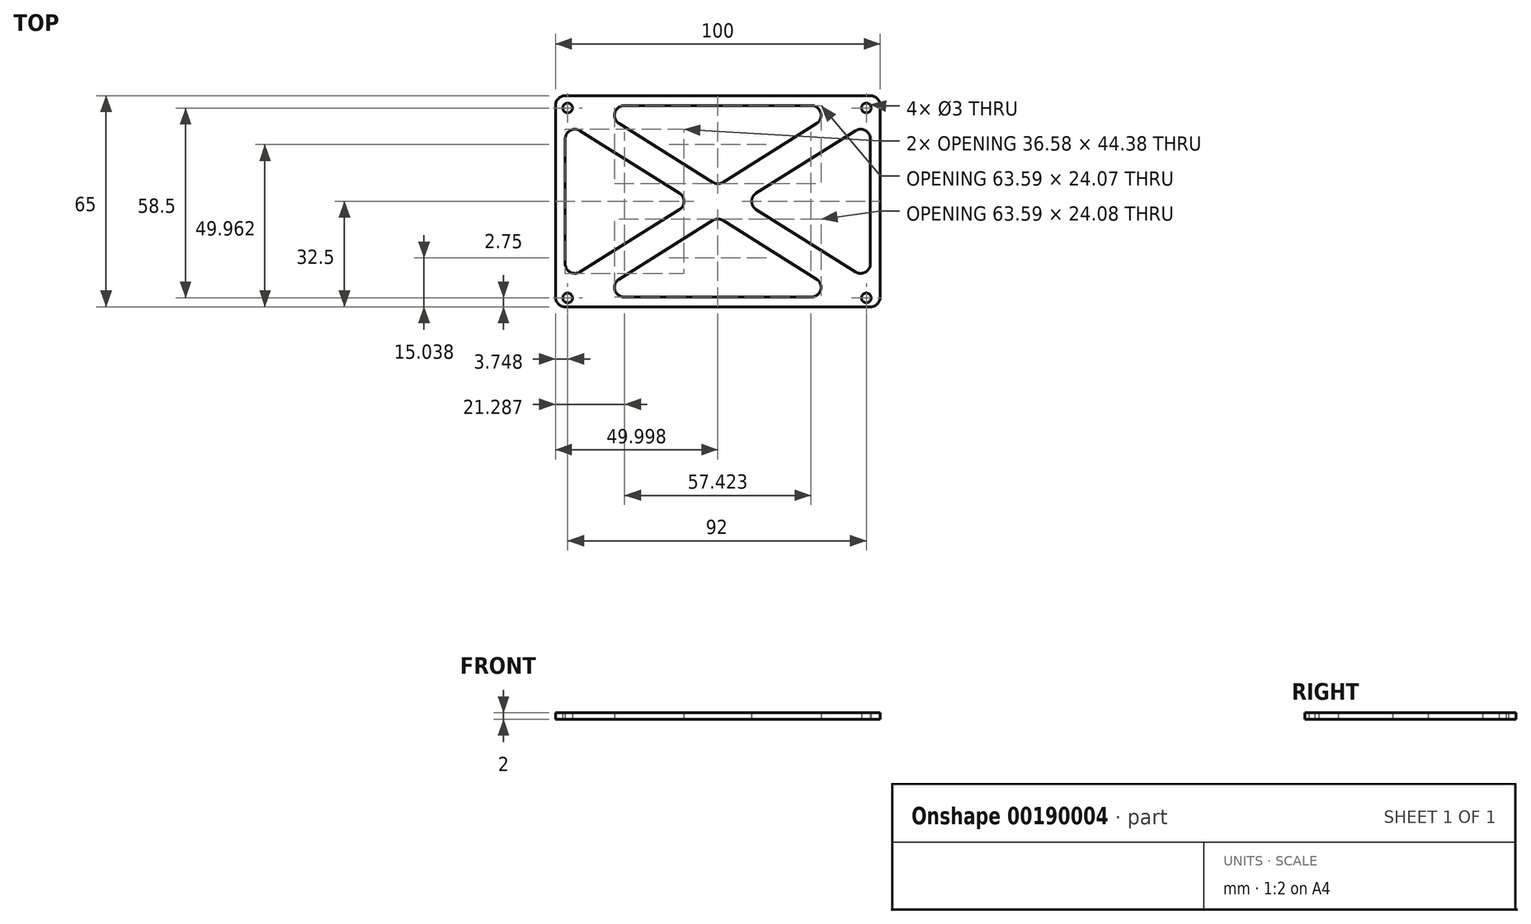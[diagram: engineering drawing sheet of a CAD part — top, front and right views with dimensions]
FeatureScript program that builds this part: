
annotation { "Feature Type Name" : "Feature", "Feature Type Description" : "" }
export const myFeature = defineFeature(function(context is Context, id is Id, definition is map)
    precondition{}
    {
        {
            var Q0;
            Q0=qCreatedBy(makeId("Top.planeOp"),FACE);
            var sketch = newSketch(context, id + "F0", { "sketchPlane" : qUnion([Q0])});
            skCircle(sketch, "E0", {"center": v(-51.9, 0) * mm, "radius": 1.5 * mm});
            skCircle(sketch, "E1", {"center": v(40.1, 0) * mm, "radius": 1.5 * mm});
            skCircle(sketch, "E2", {"center": v(-51.9, -58.5) * mm, "radius": 1.5 * mm});
            skCircle(sketch, "E3", {"center": v(40.1, -58.5) * mm, "radius": 1.5 * mm});
            skLineSegment(sketch, "E4", {"start": v(-52.65, 3.75) * mm, "end": v(-49.65, 3.75) * mm});
            skLineSegment(sketch, "E5", {"start": v(44.35, 0.75) * mm, "end": v(44.35, -2.25) * mm});
            skLineSegment(sketch, "E6", {"start": v(41.35, -61.25) * mm, "end": v(38.35, -61.25) * mm});
            skLineSegment(sketch, "E7", {"start": v(-55.65, -58.25) * mm, "end": v(-55.65, -55.25) * mm});
            skPoint(sketch, "E8.visualSharp", {"position": v(-55.65, 3.75) * mm});
            skArc(sketch, "E8.filletArc", {"start": v(-52.65, 3.75) * mm, "mid": v(-54.77, 2.87) * mm, "end": v(-55.65, 0.75) * mm});
            skPoint(sketch, "E9.visualSharp", {"position": v(44.35, 3.75) * mm});
            skArc(sketch, "E9.filletArc", {"start": v(44.35, 0.75) * mm, "mid": v(43.47, 2.87) * mm, "end": v(41.35, 3.75) * mm});
            skPoint(sketch, "E10.visualSharp", {"position": v(44.35, -61.25) * mm});
            skArc(sketch, "E10.filletArc", {"start": v(41.35, -61.25) * mm, "mid": v(43.47, -60.37) * mm, "end": v(44.35, -58.25) * mm});
            skPoint(sketch, "E11.visualSharp", {"position": v(-55.65, -61.25) * mm});
            skArc(sketch, "E11.filletArc", {"start": v(-55.65, -58.25) * mm, "mid": v(-54.77, -60.37) * mm, "end": v(-52.65, -61.25) * mm});
            skLineSegment(sketch, "E12", {"start": v(-36.04, -4.8) * mm, "end": v(-7.25, -22.87) * mm});
            skLineSegment(sketch, "E13", {"start": v(-48.06, -7.02) * mm, "end": v(-17.48, -26.2) * mm});
            skLineSegment(sketch, "E14", {"start": v(-48.06, -50.48) * mm, "end": v(-17.48, -31.3) * mm});
            skLineSegment(sketch, "E15", {"start": v(-36.04, -52.7) * mm, "end": v(-7.25, -34.63) * mm});
            skLineSegment(sketch, "E16.trimOffspring", {"start": v(-4.06, -22.87) * mm, "end": v(24.74, -4.8) * mm});
            skLineSegment(sketch, "E17.trimOffspring", {"start": v(6.18, -31.3) * mm, "end": v(36.75, -50.48) * mm});
            skLineSegment(sketch, "E18.trimOffspring", {"start": v(6.18, -26.2) * mm, "end": v(36.75, -7.02) * mm});
            skLineSegment(sketch, "E19.trimOffspring", {"start": v(-4.06, -34.63) * mm, "end": v(24.74, -52.7) * mm});
            skPoint(sketch, "E20.visualSharp", {"position": v(-13.43, -28.75) * mm});
            skArc(sketch, "E20.filletArc", {"start": v(-17.48, -31.3) * mm, "mid": v(-16.07, -28.75) * mm, "end": v(-17.48, -26.2) * mm});
            skPoint(sketch, "E21.visualSharp", {"position": v(-5.65, -33.63) * mm});
            skArc(sketch, "E21.filletArc", {"start": v(-4.06, -34.63) * mm, "mid": v(-5.65, -34.17) * mm, "end": v(-7.25, -34.63) * mm});
            skPoint(sketch, "E22.visualSharp", {"position": v(2.13, -28.75) * mm});
            skArc(sketch, "E22.filletArc", {"start": v(6.18, -26.2) * mm, "mid": v(4.77, -28.75) * mm, "end": v(6.18, -31.3) * mm});
            skPoint(sketch, "E23.visualSharp", {"position": v(-5.65, -23.87) * mm});
            skArc(sketch, "E23.filletArc", {"start": v(-7.25, -22.87) * mm, "mid": v(-5.65, -23.33) * mm, "end": v(-4.06, -22.87) * mm});
            skLineSegment(sketch, "E24.trimOffspring", {"start": v(-55.65, -2.25) * mm, "end": v(-55.65, 0.75) * mm});
            skLineSegment(sketch, "E25.trimOffspring", {"start": v(-49.65, -61.25) * mm, "end": v(-52.65, -61.25) * mm});
            skLineSegment(sketch, "E26.trimOffspring", {"start": v(38.35, 3.75) * mm, "end": v(41.35, 3.75) * mm});
            skLineSegment(sketch, "E27.trimOffspring", {"start": v(44.35, -55.25) * mm, "end": v(44.35, -58.25) * mm});
            skLineSegment(sketch, "E28", {"start": v(-55.65, -55.25) * mm, "end": v(-55.65, -2.25) * mm});
            skLineSegment(sketch, "E29", {"start": v(-49.65, -61.25) * mm, "end": v(38.35, -61.25) * mm});
            skLineSegment(sketch, "E30", {"start": v(44.35, -2.25) * mm, "end": v(44.35, -55.25) * mm});
            skLineSegment(sketch, "E31", {"start": v(38.35, 3.75) * mm, "end": v(-49.65, 3.75) * mm});
            skLineSegment(sketch, "E32", {"start": v(-34.45, 0.75) * mm, "end": v(23.15, 0.75) * mm});
            skLineSegment(sketch, "E33", {"start": v(-34.45, -58.25) * mm, "end": v(23.15, -58.25) * mm});
            skLineSegment(sketch, "E34", {"start": v(41.35, -47.94) * mm, "end": v(41.35, -9.56) * mm});
            skLineSegment(sketch, "E35", {"start": v(-52.65, -47.94) * mm, "end": v(-52.65, -9.56) * mm});
            skPoint(sketch, "E36.visualSharp", {"position": v(-52.65, -4.13) * mm});
            skArc(sketch, "E36.filletArc", {"start": v(-48.06, -7.02) * mm, "mid": v(-51.1, -6.93) * mm, "end": v(-52.65, -9.56) * mm});
            skPoint(sketch, "E37.visualSharp", {"position": v(-44.87, 0.75) * mm});
            skArc(sketch, "E37.filletArc", {"start": v(-34.45, 0.75) * mm, "mid": v(-37.33, -1.42) * mm, "end": v(-36.04, -4.8) * mm});
            skPoint(sketch, "E38.visualSharp", {"position": v(33.57, 0.75) * mm});
            skArc(sketch, "E38.filletArc", {"start": v(24.74, -4.8) * mm, "mid": v(26.03, -1.42) * mm, "end": v(23.15, 0.75) * mm});
            skPoint(sketch, "E39.visualSharp", {"position": v(41.35, -4.13) * mm});
            skArc(sketch, "E39.filletArc", {"start": v(41.35, -9.56) * mm, "mid": v(39.8, -6.93) * mm, "end": v(36.75, -7.02) * mm});
            skPoint(sketch, "E40.visualSharp", {"position": v(41.35, -53.37) * mm});
            skArc(sketch, "E40.filletArc", {"start": v(36.75, -50.48) * mm, "mid": v(39.8, -50.57) * mm, "end": v(41.35, -47.94) * mm});
            skPoint(sketch, "E41.visualSharp", {"position": v(33.57, -58.25) * mm});
            skArc(sketch, "E41.filletArc", {"start": v(23.15, -58.25) * mm, "mid": v(26.03, -56.08) * mm, "end": v(24.74, -52.7) * mm});
            skPoint(sketch, "E42.visualSharp", {"position": v(-44.87, -58.25) * mm});
            skArc(sketch, "E42.filletArc", {"start": v(-36.04, -52.7) * mm, "mid": v(-37.33, -56.08) * mm, "end": v(-34.45, -58.25) * mm});
            skPoint(sketch, "E43.visualSharp", {"position": v(-52.65, -53.37) * mm});
            skArc(sketch, "E43.filletArc", {"start": v(-52.65, -47.94) * mm, "mid": v(-51.1, -50.57) * mm, "end": v(-48.06, -50.48) * mm});
            skSolve(sketch);
        }
        {
            var Q0;
            Q0 = qSketchRegion(id + "F0", true);
            extrude(context, id + "F1", {"entities" : qUnion([Q0]), "depth" : 2 * mm});
        }
    });
